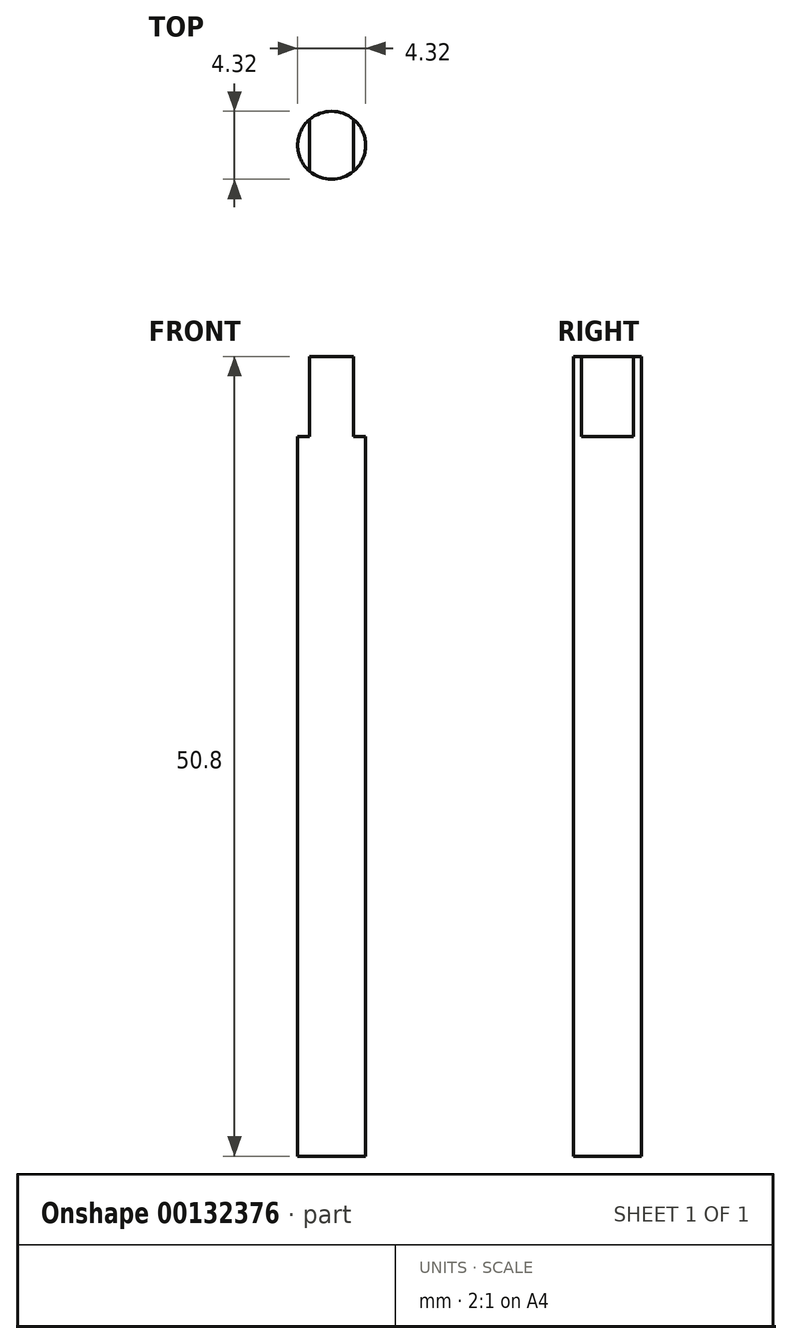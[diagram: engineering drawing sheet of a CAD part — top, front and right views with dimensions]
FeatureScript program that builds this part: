
annotation { "Feature Type Name" : "Feature", "Feature Type Description" : "" }
export const myFeature = defineFeature(function(context is Context, id is Id, definition is map)
    precondition{}
    {
        {
            var Q0;
            Q0=qCreatedBy(makeId("Top.planeOp"),FACE);
            var sketch = newSketch(context, id + "F0", { "sketchPlane" : qUnion([Q0])});
            skCircle(sketch, "E0", {"center": v(0, 0) * mm, "radius": 2.16 * mm});
            skSolve(sketch);
        }
        {
            var Q0;
            Q0=makeQuery(id+"F0.imprint","IMPRINT",FACE,{"disambiguationData":[TD([[makeQuery(id+"F0.imprint","IMPRINT",EDGE,{"derivedFrom":sQuery(id+"F0.wireOp",EDGE,"E0")}),1.0]])]});
            extrude(context, id + "F1", {"entities" : qUnion([Q0]), "depth" : 50.8 * mm});
        }
        {
            var Q0;
            Q0=makeQuery(id+"F1.opExtrude","CAP_FACE",FACE,{"disambiguationData":[OSD([sQuery(id+"F0.wireOp",EDGE,"E0")])],"isStart":false});
            var sketch = newSketch(context, id + "F2", { "sketchPlane" : qUnion([Q0])});
            skLineSegment(sketch, "E1", {"start": v(-1.4, 1.65) * mm, "end": v(-1.4, -1.65) * mm});
            skLineSegment(sketch, "E2.MirrorCS", {"start": v(1.4, 1.65) * mm, "end": v(1.4, -1.65) * mm});
            skArc(sketch, "E3", {"start": v(1.4, -1.65) * mm, "mid": v(2.18, 0) * mm, "end": v(1.4, 1.65) * mm});
            skArc(sketch, "E4.MirrorCS", {"start": v(-1.4, -1.65) * mm, "mid": v(-2.18, 0) * mm, "end": v(-1.4, 1.65) * mm});
            skSolve(sketch);
        }
        {
            var Q0;
            {var subQ0=sQuery(id+"F2.wireOp",EDGE,"E2.MirrorCS");Q0=makeQuery(id+"F2.imprint","IMPRINT",FACE,{"disambiguationData":[TD([[makeQuery(id+"F2.imprint","IMPRINT",EDGE,{"derivedFrom":subQ0}),1.0]])]});}
            var Q1;
            Q1=makeQuery(id+"F2.imprint","IMPRINT",FACE,{"disambiguationData":[TD([[makeQuery(id+"F2.imprint","IMPRINT",EDGE,{"derivedFrom":sQuery(id+"F2.wireOp",EDGE,"E1")}),-1.0]])]});
            extrude(context, id + "F3", {"entities" : qUnion([Q0, Q1]), "operationType" : NewBodyOperationType.REMOVE, "oppositeDirection" : true, "depth" : 5.08 * mm});
        }
    });
